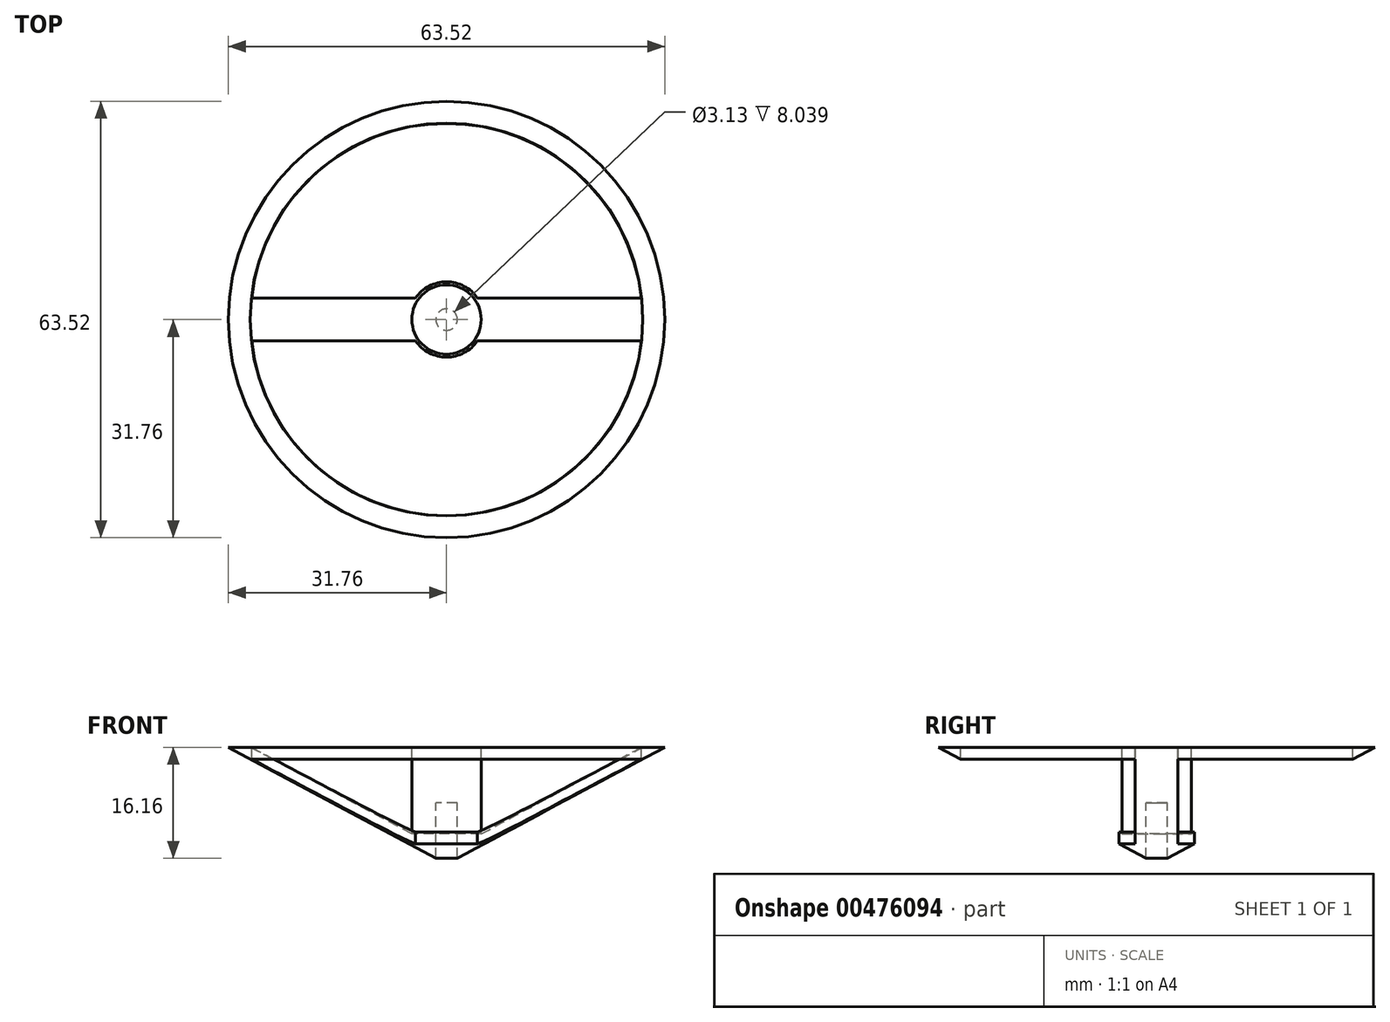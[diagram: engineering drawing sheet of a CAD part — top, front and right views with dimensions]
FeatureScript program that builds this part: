
annotation { "Feature Type Name" : "Feature", "Feature Type Description" : "" }
export const myFeature = defineFeature(function(context is Context, id is Id, definition is map)
    precondition{}
    {
        {
            var Q0;
            Q0=qCreatedBy(makeId("Front.planeOp"),FACE);
            var sketch = newSketch(context, id + "F0", { "sketchPlane" : qUnion([Q0])});
            skLineSegment(sketch, "E0", {"start": v(0, 0) * mm, "end": v(0, -8.12) * mm});
            skLineSegment(sketch, "E1", {"start": v(31.76, 0) * mm, "end": v(28.58, 0) * mm});
            skLineSegment(sketch, "E2.left", {"start": v(0, -8.12) * mm, "end": v(0, -7.36) * mm});
            skLineSegment(sketch, "E3", {"start": v(31.76, 0) * mm, "end": v(4.72, -14.47) * mm});
            skLineSegment(sketch, "E4", {"start": v(0, -8.12) * mm, "end": v(1.57, -8.12) * mm});
            skLineSegment(sketch, "E5", {"start": v(1.57, -8.12) * mm, "end": v(1.57, -16.16) * mm});
            skLineSegment(sketch, "E6", {"start": v(1.57, -16.16) * mm, "end": v(4.72, -14.47) * mm});
            skLineSegment(sketch, "E7", {"start": v(0, 0) * mm, "end": v(4.52, 0) * mm});
            skLineSegment(sketch, "E8", {"start": v(0, 0) * mm, "end": v(5.05, 0) * mm});
            skPoint(sketch, "E8.endSnap0", {"position": v(2.26, 0) * mm});
            skLineSegment(sketch, "E9", {"start": v(1.57, -16.16) * mm, "end": v(1.57, -14.47) * mm});
            skLineSegment(sketch, "E10", {"start": v(5.05, 0) * mm, "end": v(5.05, -12.6) * mm});
            skLineSegment(sketch, "E11", {"start": v(5.05, -12.6) * mm, "end": v(28.58, 0) * mm});
            skSolve(sketch);
        }
        {
            var Q0;
            Q0=makeQuery(id+"F0.imprint","IMPRINT",FACE,{"disambiguationData":[TD([[makeQuery(id+"F0.imprint","IMPRINT",EDGE,{"derivedFrom":sQuery(id+"F0.wireOp",EDGE,"E0")}),1.0]])]});
            var Q1;
            Q1=sQuery(id+"F0.wireOp",EDGE,"E0");
            revolve(context, id + "F1", {"entities" : qUnion([Q0]), "axis" : qUnion([Q1]), "revolveType" : RevolveType.FULL});
        }
        {
            var Q0;
            Q0=qCreatedBy(makeId("Top.planeOp"),FACE);
            var sketch = newSketch(context, id + "F2", { "sketchPlane" : qUnion([Q0])});
            skCircle(sketch, "E12", {"center": v(0, 0) * mm, "radius": 5.48 * mm});
            skLineSegment(sketch, "E13", {"start": v(-28.38, 3.1) * mm, "end": v(-4.51, 3.1) * mm});
            skLineSegment(sketch, "E14", {"start": v(-28.38, -3.1) * mm, "end": v(-4.51, -3.1) * mm});
            skLineSegment(sketch, "E15", {"start": v(28.38, 3.1) * mm, "end": v(4.51, 3.1) * mm});
            skLineSegment(sketch, "E16", {"start": v(28.38, -3.1) * mm, "end": v(4.51, -3.1) * mm});
            skArc(sketch, "E17", {"start": v(-28.38, 3.1) * mm, "mid": v(0, 28.55) * mm, "end": v(28.38, 3.1) * mm});
            skArc(sketch, "E18", {"start": v(28.38, -3.1) * mm, "mid": v(0, -28.55) * mm, "end": v(-28.38, -3.1) * mm});
            skSolve(sketch);
        }
        {
            var Q0;
            {var subQ0=sQuery(id+"F2.wireOp",EDGE,"E13");Q0=makeQuery(id+"F2.imprint","IMPRINT",FACE,{"disambiguationData":[TD([[makeQuery(id+"F2.imprint","IMPRINT",EDGE,{"derivedFrom":subQ0}),1.0]])]});}
            var Q1;
            {var subQ0=sQuery(id+"F2.wireOp",EDGE,"E14");Q1=makeQuery(id+"F2.imprint","IMPRINT",FACE,{"disambiguationData":[TD([[makeQuery(id+"F2.imprint","IMPRINT",EDGE,{"derivedFrom":subQ0}),-1.0]])]});}
            extrude(context, id + "F3", {"entities" : qUnion([Q0, Q1]), "operationType" : NewBodyOperationType.REMOVE, "oppositeDirection" : true, "depth" : 25.4 * mm});
        }
    });
